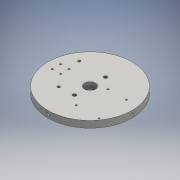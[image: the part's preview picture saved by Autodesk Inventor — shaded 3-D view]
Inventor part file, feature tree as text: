
AUTODESK INVENTOR PART (.ipt)
format: ipt  version: 2016 (Build 200138000, 138)  size: 195,584 bytes
history: native  units: mm
features: extrude x9, sketch x8, thread x6, other x5
ambient origin geometry x8: Origin, YZ Plane, XZ Plane, XY Plane, X Axis, Y Axis, Z Axis, Center Point
bodies: Body1 (feature_tree)
feature tree (28):
  other  "ソリッド1"
  extrude  "押し出し1"  Depth=100.0mm
  other  "作業平面1"
  other  "作業平面2"
  other  "作業平面3"
  other  "作業平面4"
  extrude  "押し出し2"  Depth=8.0mm TaperAngle=0.0deg
  extrude  "押し出し3"  Depth=50.0mm
  extrude  "押し出し4"  Depth=4.0mm
  extrude  "押し出し5"  Depth=3.0mm
  thread  "ねじ1"
  thread  "ねじ2"
  thread  "ねじ3"
  thread  "ねじ4"
  extrude  "押し出し7"  Depth=5.0mm TaperAngle=0.0deg
  thread  "ねじ7"
  thread  "ねじ8"
  sketch  "スケッチ9"
  extrude  "押し出し10"  Depth=4.0mm
  extrude  "押し出し11"  Depth=3.0mm
  extrude  "押し出し12"  Depth=5.0mm TaperAngle=0.0deg
  sketch  "スケッチ1"
  sketch  "スケッチ2"
  sketch  "スケッチ3"
  sketch  "スケッチ4"
  sketch  "スケッチ5"
  sketch  "スケッチ10"
  sketch  "スケッチ13"
